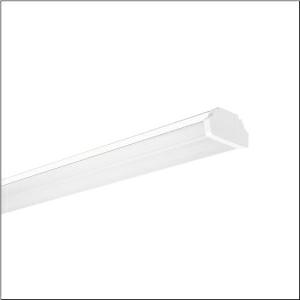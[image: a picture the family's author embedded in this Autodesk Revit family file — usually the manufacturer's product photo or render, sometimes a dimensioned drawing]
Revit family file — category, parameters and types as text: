
# Revit family: dus_31_gen_2_53bd812dv4d5d23sl3_8c21
name_source: partatom
category: Lighting Fixtures
units: mm (PartAtom-declared; Revit-internal decimal feet)

## family parameters
Cut with Voids When Loaded = No
Host = Face
Light Source = No
Part Type = Normal
Room Calculation Point = No
Round Connector Dimension = Use Diameter
Shared = No

## types (1)
- --- (1 x LED, 940 lm, 7.5 W, 4000K)
    Apparent Load = 8 VA
    CIE Flux Codes = 47 80 95 93 100
    Color Rendering = 80
    Color Temperature = 4000K
    Default Elevation = 1800 mm
    Description = DUS 31 Gen.2, luminaire insert, of sheet steel, coil coated, white, length: 1.535mm, width: 81mm, height: 90mm, 5x system unit, system units: 307mm, LED rated luminous flux: 13.680lm, light colour: 840, SDCM (Standard Deviation of Colour Matching)MacAdam ≤ 3 SDCM (initial), control gear: DALI 2, with plug, 6-pole, with phase selection (L1, L2), mains connection: 220..240V, AC, 50/60Hz, rated input power: 79W, for emergency light function, charging phase on L3 (wire number 3), through-wiring accessed according to module size, converter,control gear: single battery element, battery: LiFePO4, 9Ah, primary optical cover: cover, of PMMA, light emission: direct distribution, primary light characteristic: symmetric, protection rating (complete): IP20, protection rating (LED compartment): IP50, insulation class (complete): insulation class I (protective earthing), certification: CE, UKCA, impact resistance: IK03, permissible ambient temperature for indoor applications: +5..+35°C, standard: EN 60598-2-22, corresponds to IFS (International Featured Standards) requirements for safety and quality in the food industry, reducing of maximum allowable ambient temperature of 5°C with ceiling mounting, packaging unit: 1 piece
    Height = 95 mm
    Lamp = 1 x LED
    Lamp Light Flux = 940 lm
    Lamp Power = 7.5 W
    Lamp count = 1
    Length = 1535 mm
    Luminous efficacy = 125 lm/W
    Manufacturer = Siteco
    ModVariant = No
    Model = 53BD812DV4D5D23SL3
    Mounting Place = Ceiling
    Mounting Type = Pendant
    Number of Poles = 1
    OnlyDefault = Yes
    Power Factor = 1
    Product Name = DUS 31 Gen.2
    Product group = luminaire insert | ceiling pendant
    ProductGroupID = 901
    Protection Class = Protection class I
    Protection Degree = IP 20
    RLX_Detail_Level = 1
    RLX_Emergency_Light_Flux = 0 lm
    RLX_Emergency_Type = 0
    RLX_Emergency_Type_DB = No
    RlxData = <blob elided: 32633 chars, md5=1bfcffe5>
    Socket = socket
    Standby Power = 0 W
    System Light Flux = 940 lm
    System Power = 8 W
    Type Comments = : emergency light operation: 3 h
    Type Image = l_1319596.jpg
    URL = http://relux.com
    VarID = @adj_038567
    Voltage = 0 V
    Weight = 0.00 kg
    Width = 81 mm

## geometry (parser evidence)
native form markers: Blend x4, Sweep x16
no freeform markers — native parametric forms only
